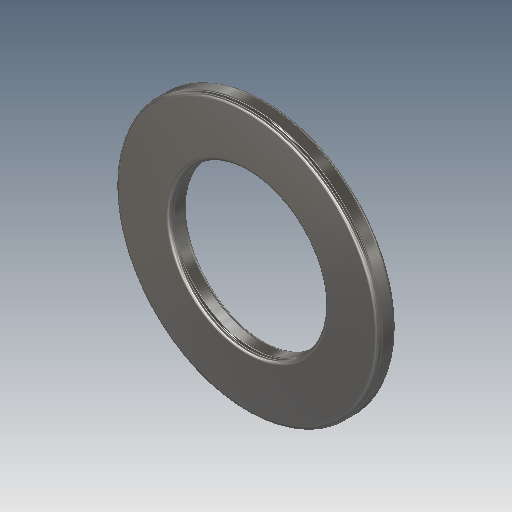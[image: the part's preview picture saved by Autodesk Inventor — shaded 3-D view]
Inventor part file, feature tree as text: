
AUTODESK INVENTOR PART (.ipt)
format: ipt  version: 2018 (Build 220112000, 112)  size: 155,136 bytes
history: native  units: mm
features: extrude x1, fillet x1, sketch x1
ambient origin geometry x8: Origin, YZ Plane, XZ Plane, XY Plane, X Axis, Y Axis, Z Axis, Center Point
bodies: Solid1 (feature_tree)
feature tree (3):
  extrude  "Extrusion1"  Depth=0.5mm
  fillet  "Fillet1"  Radius=2.0mm
  sketch  "Sketch1"  dims[d0=29.0mm d1=16.8mm d2=2.0mm d3=0.0mm d4=0.5mm]
